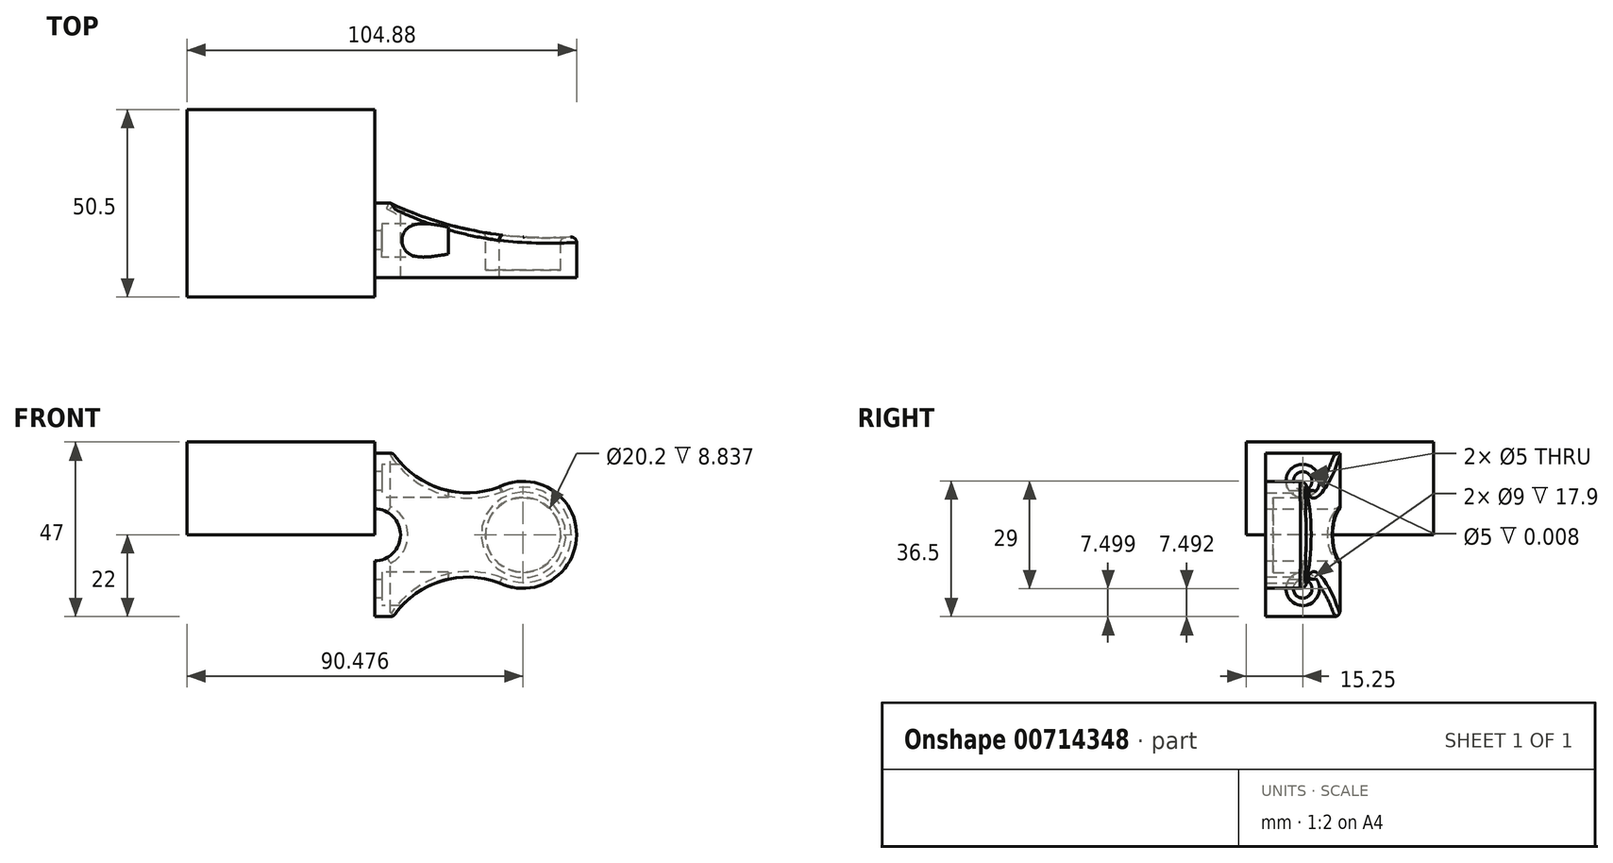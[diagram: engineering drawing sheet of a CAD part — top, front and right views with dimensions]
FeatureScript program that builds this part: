
annotation { "Feature Type Name" : "Feature", "Feature Type Description" : "" }
export const myFeature = defineFeature(function(context is Context, id is Id, definition is map)
    precondition{}
    {
        {
            var Q0;
            Q0=qCreatedBy(makeId("Top.planeOp"),FACE);
            var sketch = newSketch(context, id + "F0", { "sketchPlane" : qUnion([Q0])});
            skLineSegment(sketch, "E0.bottom", {"start": v(25.25, 25.25) * mm, "end": v(-25.25, 25.25) * mm});
            skLineSegment(sketch, "E0.top", {"start": v(25.25, -25.25) * mm, "end": v(-25.25, -25.25) * mm});
            skLineSegment(sketch, "E0.left", {"start": v(25.25, 25.25) * mm, "end": v(25.25, -25.25) * mm});
            skLineSegment(sketch, "E0.right", {"start": v(-25.25, 25.25) * mm, "end": v(-25.25, -25.25) * mm});
            skPoint(sketch, "E0.middle", {"position": v(0, 0) * mm});
            skSolve(sketch);
        }
        {
            var Q0;
            Q0 = qSketchRegion(id + "F0", true);
            extrude(context, id + "F1", {"entities" : qUnion([Q0]), "depth" : 25 * mm, "offsetDistance" : 25 * mm});
        }
        {
            var Q0;
            Q0=qCreatedBy(makeId("Front.planeOp"),FACE);
            var sketch = newSketch(context, id + "F2", { "sketchPlane" : qUnion([Q0])});
            skLineSegment(sketch, "E1.top", {"start": v(25.25, 22) * mm, "end": v(71.34, 22) * mm});
            skCircle(sketch, "E2", {"center": v(65.23, 0) * mm, "radius": 10.1 * mm});
            skLineSegment(sketch, "E3", {"start": v(25.25, 22) * mm, "end": v(30.25, 22) * mm});
            skLineSegment(sketch, "E4", {"start": v(79.63, 0) * mm, "end": v(75.33, 0) * mm});
            skArc(sketch, "E5", {"start": v(32.23, 0) * mm, "mid": v(30.18, 4.94) * mm, "end": v(25.24, 7) * mm});
            skLineSegment(sketch, "E6", {"start": v(25.23, 0) * mm, "end": v(32.23, 0) * mm});
            skLineSegment(sketch, "E7", {"start": v(25.24, 7) * mm, "end": v(25.25, 22) * mm});
            skArc(sketch, "E8.MirrorCS", {"start": v(79.63, 0) * mm, "mid": v(72.81, -12.24) * mm, "end": v(58.82, -12.9) * mm});
            skArc(sketch, "E9.MirrorCS", {"start": v(32.23, 0) * mm, "mid": v(30.18, -4.94) * mm, "end": v(25.24, -7) * mm});
            skArc(sketch, "E10.MirrorCS", {"start": v(30.25, -22) * mm, "mid": v(42.95, -12.48) * mm, "end": v(58.82, -12.9) * mm});
            skLineSegment(sketch, "E11.MirrorCS", {"start": v(25.24, -7) * mm, "end": v(25.25, -22) * mm});
            skLineSegment(sketch, "E12.MirrorCS", {"start": v(25.25, -22) * mm, "end": v(30.25, -22) * mm});
            skArc(sketch, "E13.MirrorCS", {"start": v(30.25, 22) * mm, "mid": v(42.95, 12.48) * mm, "end": v(58.82, 12.9) * mm});
            skArc(sketch, "E14.MirrorCS", {"start": v(79.63, 0) * mm, "mid": v(72.81, 12.24) * mm, "end": v(58.82, 12.9) * mm});
            skSolve(sketch);
        }
        {
            var Q0;
            Q0=makeQuery(id+"F2.imprint","IMPRINT",FACE,{"disambiguationData":[TD([[makeQuery(id+"F2.imprint","IMPRINT",EDGE,{"derivedFrom":sQuery(id+"F2.wireOp",EDGE,"E2")}),-1.0]])]});
            extrude(context, id + "F3", {"entities" : qUnion([Q0]), "depth" : 20 * mm, "offsetDistance" : 25 * mm});
        }
        {
            var Q0;
            Q0=makeQuery(id+"F2.imprint","IMPRINT",FACE,{"disambiguationData":[TD([[makeQuery(id+"F2.imprint","IMPRINT",EDGE,{"derivedFrom":sQuery(id+"F2.wireOp",EDGE,"E2")}),1.0]])]});
            extrude(context, id + "F4", {"entities" : qUnion([Q0]), "operationType" : NewBodyOperationType.ADD, "depth" : 20 * mm, "offsetDistance" : 25 * mm, "hasSecondDirection" : true, "secondDirectionOppositeDirection" : false, "secondDirectionDepth" : 18 * mm});
        }
        {
            var Q0;
            Q0=qCreatedBy(makeId("Top.planeOp"),FACE);
            var sketch = newSketch(context, id + "F5", { "sketchPlane" : qUnion([Q0])});
            skArc(sketch, "E15", {"start": v(29.47, 0) * mm, "mid": v(54.91, -7.9) * mm, "end": v(81.54, -8.81) * mm});
            skLineSegment(sketch, "E16", {"start": v(29.47, 0) * mm, "end": v(29.47, 7.06) * mm});
            skLineSegment(sketch, "E17", {"start": v(29.47, 7.06) * mm, "end": v(81.54, 7.06) * mm});
            skLineSegment(sketch, "E18", {"start": v(81.54, 7.06) * mm, "end": v(81.54, -8.81) * mm});
            skSolve(sketch);
        }
        {
            var Q0;
            Q0=makeQuery(id+"F5.imprint","IMPRINT",FACE,{"disambiguationData":[TD([[makeQuery(id+"F5.imprint","IMPRINT",EDGE,{"derivedFrom":sQuery(id+"F5.wireOp",EDGE,"E15")}),1.0]])]});
            extrude(context, id + "F6", {"entities" : qUnion([Q0]), "operationType" : NewBodyOperationType.REMOVE, "oppositeDirection" : true, "depth" : 25 * mm, "offsetDistance" : 25 * mm, "hasSecondDirection" : true, "secondDirectionOppositeDirection" : false, "secondDirectionDepth" : 25 * mm});
        }
        {
            var Q0;
            Q0=makeQuery(id+"F3.opExtrude","SWEPT_FACE",FACE,{"disambiguationData":[OSD([sQuery(id+"F2.wireOp",EDGE,"E7")])]});
            var sketch = newSketch(context, id + "F7", { "sketchPlane" : qUnion([Q0])});
            skCircle(sketch, "E19", {"center": v(10, -14.48) * mm, "radius": 2.5 * mm});
            skPoint(sketch, "E19.centerSnap0", {"position": v(0, -14.48) * mm});
            skPoint(sketch, "E19.centerSnap1", {"position": v(10, -21.98) * mm});
            skCircle(sketch, "E20.0", {"center": v(10, -14.48) * mm, "radius": 4.5 * mm});
            skCircle(sketch, "E21.0", {"center": v(10, 14.52) * mm, "radius": 4.5 * mm});
            skPoint(sketch, "E22", {"position": v(10, 22.02) * mm});
            skPoint(sketch, "E23", {"position": v(0, 14.52) * mm});
            skCircle(sketch, "E24", {"center": v(10, 14.52) * mm, "radius": 2.5 * mm});
            skSolve(sketch);
        }
        {
            var Q0;
            Q0=makeQuery(id+"F7.imprint","IMPRINT",FACE,{"disambiguationData":[TD([[makeQuery(id+"F7.imprint","IMPRINT",EDGE,{"derivedFrom":sQuery(id+"F7.wireOp",EDGE,"E24")}),1.0]])]});
            var Q1;
            Q1=makeQuery(id+"F7.imprint","IMPRINT",FACE,{"disambiguationData":[TD([[makeQuery(id+"F7.imprint","IMPRINT",EDGE,{"derivedFrom":sQuery(id+"F7.wireOp",EDGE,"E19")}),1.0]])]});
            extrude(context, id + "F8", {"entities" : qUnion([Q0, Q1]), "operationType" : NewBodyOperationType.REMOVE, "oppositeDirection" : true, "depth" : 25 * mm, "offsetDistance" : 25 * mm});
        }
        {
            var Q0;
            Q0=makeQuery(id+"F7.imprint","IMPRINT",FACE,{"disambiguationData":[TD([[makeQuery(id+"F7.imprint","IMPRINT",EDGE,{"derivedFrom":sQuery(id+"F7.wireOp",EDGE,"E21.0")}),1.0]])]});
            var Q1;
            Q1=makeQuery(id+"F7.imprint","IMPRINT",FACE,{"disambiguationData":[TD([[makeQuery(id+"F7.imprint","IMPRINT",EDGE,{"derivedFrom":sQuery(id+"F7.wireOp",EDGE,"E19")}),-1.0]])]});
            extrude(context, id + "F9", {"entities" : qUnion([Q0, Q1]), "operationType" : NewBodyOperationType.REMOVE, "oppositeDirection" : true, "depth" : 19.9 * mm, "offsetDistance" : 25 * mm, "hasSecondDirection" : true, "secondDirectionOppositeDirection" : false, "secondDirectionDepth" : -2 * mm});
        }
        {
            var Q0;
            Q0=makeQuery(id+"F6.boolean.opBoolean","INTERSECT",EDGE,{"derivedFrom":[makeQuery(id+"F3.opExtrude","SWEPT_FACE",FACE,{"disambiguationData":[OSD([sQuery(id+"F2.wireOp",EDGE,"E10.MirrorCS")])]}),makeQuery(id+"F6.opExtrude","SWEPT_FACE",FACE,{"disambiguationData":[OSD([sQuery(id+"F5.wireOp",EDGE,"E15")])]})]});
            var Q1;
            Q1=makeQuery(id+"F6.boolean.opBoolean","INTERSECT",EDGE,{"derivedFrom":[makeQuery(id+"F3.opExtrude","SWEPT_FACE",FACE,{"disambiguationData":[OSD([sQuery(id+"F2.wireOp",EDGE,"E13.MirrorCS")])]}),makeQuery(id+"F6.opExtrude","SWEPT_FACE",FACE,{"disambiguationData":[OSD([sQuery(id+"F5.wireOp",EDGE,"E15")])]})]});
            var Q2;
            Q2=makeQuery(id+"F6.boolean.opBoolean","INTERSECT",EDGE,{"derivedFrom":[makeQuery(id+"F3.opExtrude","SWEPT_FACE",FACE,{"disambiguationData":[OSD([sQuery(id+"F2.wireOp",EDGE,"E8.MirrorCS"),sQuery(id+"F2.wireOp",EDGE,"E14.MirrorCS")])]}),makeQuery(id+"F6.opExtrude","SWEPT_FACE",FACE,{"disambiguationData":[OSD([sQuery(id+"F5.wireOp",EDGE,"E15")])]})]});
            var Q3;
            Q3=makeQuery(id+"F3.opExtrude","SWEPT_EDGE",EDGE,{"disambiguationData":[OSD([sQuery(id+"F2.wireOp",EDGE,"E3"),sQuery(id+"F2.wireOp",EDGE,"E13.MirrorCS")])]});
            var Q4;
            Q4=makeQuery(id+"F3.opExtrude","SWEPT_EDGE",EDGE,{"disambiguationData":[OSD([sQuery(id+"F2.wireOp",EDGE,"E10.MirrorCS"),sQuery(id+"F2.wireOp",EDGE,"E12.MirrorCS")])]});
            var Q5;
            Q5=makeQuery(id+"F3.opExtrude","CAP_EDGE",EDGE,{"disambiguationData":[OSD([sQuery(id+"F2.wireOp",EDGE,"E12.MirrorCS")])],"isStart":true});
            var Q6;
            Q6=makeQuery(id+"F3.opExtrude","CAP_EDGE",EDGE,{"disambiguationData":[OSD([sQuery(id+"F2.wireOp",EDGE,"E3")])],"isStart":true});
            var Q7;
            Q7=makeQuery(id+"F6.boolean.opBoolean","INTERSECT",EDGE,{"derivedFrom":[makeQuery(id+"F3.opExtrude","SWEPT_FACE",FACE,{"disambiguationData":[OSD([sQuery(id+"F2.wireOp",EDGE,"E5"),sQuery(id+"F2.wireOp",EDGE,"E9.MirrorCS")])]}),makeQuery(id+"F6.opExtrude","SWEPT_FACE",FACE,{"disambiguationData":[OSD([sQuery(id+"F5.wireOp",EDGE,"E15")])]})]});
            var Q8;
            {var subQ0=sQuery(id+"F2.wireOp",EDGE,"E9.MirrorCS");var subQ1=sQuery(id+"F2.wireOp",EDGE,"E7");var subQ2=sQuery(id+"F2.wireOp",EDGE,"E5");Q8=makeQuery(id+"F6.boolean.opBoolean","SPLIT",EDGE,{"disambiguationData":[TD([makeQuery(id+"F3.opExtrude","SWEPT_FACE",FACE,{"disambiguationData":[OSD([subQ1])]})])],"derivedFrom":makeQuery(id+"F3.opExtrude","CAP_EDGE",EDGE,{"disambiguationData":[OSD([subQ2,subQ0])],"isStart":true})});}
            var Q9;
            {var subQ0=sQuery(id+"F2.wireOp",EDGE,"E11.MirrorCS");var subQ1=sQuery(id+"F2.wireOp",EDGE,"E9.MirrorCS");var subQ2=sQuery(id+"F2.wireOp",EDGE,"E5");Q9=makeQuery(id+"F6.boolean.opBoolean","SPLIT",EDGE,{"disambiguationData":[TD([makeQuery(id+"F3.opExtrude","SWEPT_FACE",FACE,{"disambiguationData":[OSD([subQ0])]})])],"derivedFrom":makeQuery(id+"F3.opExtrude","CAP_EDGE",EDGE,{"disambiguationData":[OSD([subQ2,subQ1])],"isStart":true})});}
            var Q10;
            Q10=makeQuery(id+"F6.boolean.opBoolean","INTERSECT",EDGE,{"derivedFrom":[makeQuery(id+"F3.opExtrude","SWEPT_FACE",FACE,{"disambiguationData":[OSD([sQuery(id+"F2.wireOp",EDGE,"E2")])]}),makeQuery(id+"F6.opExtrude","SWEPT_FACE",FACE,{"disambiguationData":[OSD([sQuery(id+"F5.wireOp",EDGE,"E15")])]})]});
            fillet(context, id + "F10", {"entities" : qUnion([Q0, Q1, Q2, Q3, Q4, Q5, Q6, Q7, Q8, Q9, Q10]), "radius" : 1.45 * mm, "tangentPropagation" : true, "allowEdgeOverflow" : false});
        }
    });
